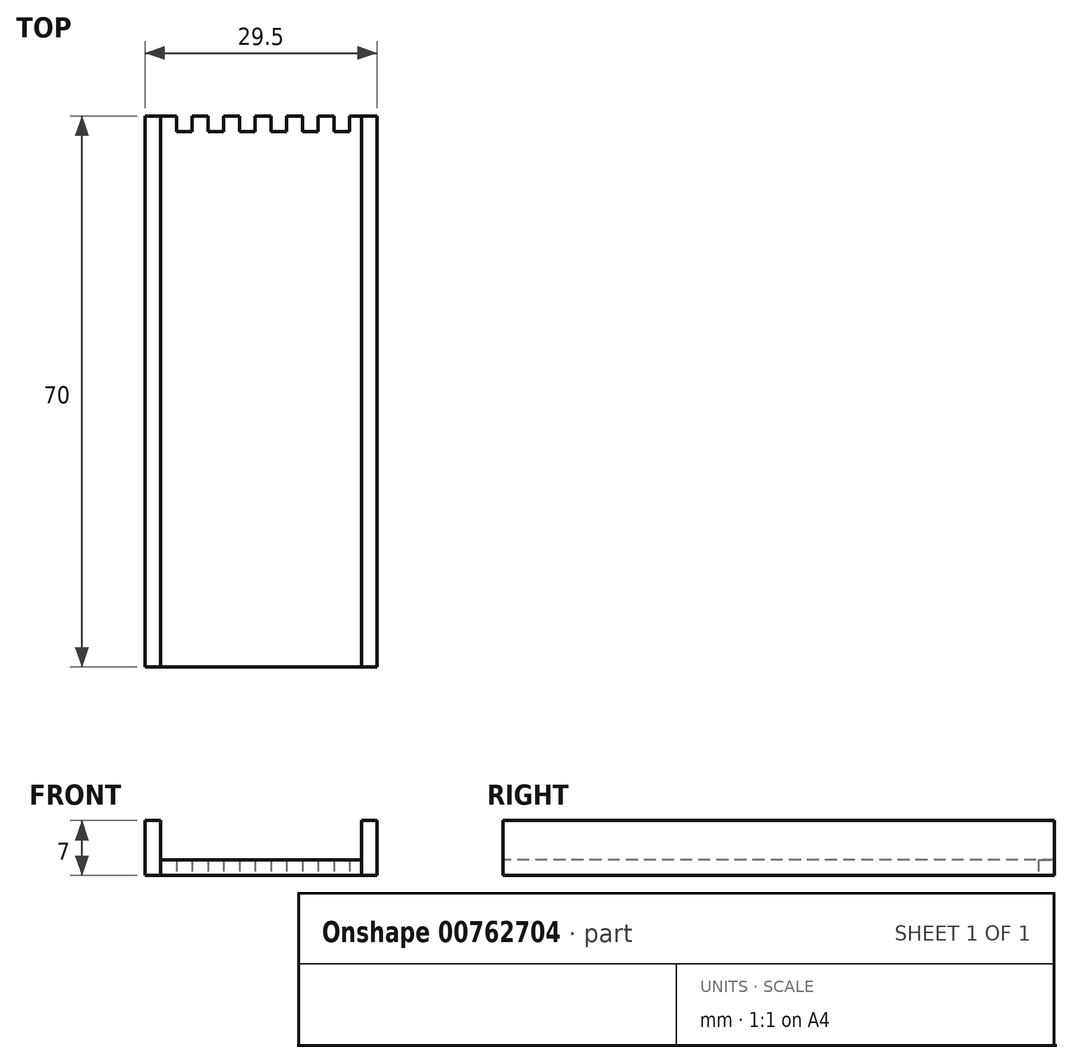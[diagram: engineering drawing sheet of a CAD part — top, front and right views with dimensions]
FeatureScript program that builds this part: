
annotation { "Feature Type Name" : "Feature", "Feature Type Description" : "" }
export const myFeature = defineFeature(function(context is Context, id is Id, definition is map)
    precondition{}
    {
        {
            var Q0;
            Q0=qCreatedBy(makeId("Top.planeOp"),FACE);
            var sketch = newSketch(context, id + "F0", { "sketchPlane" : qUnion([Q0])});
            skLineSegment(sketch, "E0.top", {"start": v(12.75, -35) * mm, "end": v(-12.75, -35) * mm});
            skLineSegment(sketch, "E0.left", {"start": v(12.75, 35) * mm, "end": v(12.75, -35) * mm});
            skLineSegment(sketch, "E0.right", {"start": v(-12.75, 35) * mm, "end": v(-12.75, -35) * mm});
            skPoint(sketch, "E0.middle", {"position": v(0, 0) * mm});
            skLineSegment(sketch, "E1", {"start": v(-12.75, 35) * mm, "end": v(-10.75, 35) * mm});
            skLineSegment(sketch, "E2", {"start": v(-10.75, 35) * mm, "end": v(-10.75, 33) * mm});
            skLineSegment(sketch, "E3", {"start": v(-10.75, 33) * mm, "end": v(-8.75, 33) * mm});
            skLineSegment(sketch, "E4", {"start": v(-8.75, 33) * mm, "end": v(-8.75, 35) * mm});
            skLineSegment(sketch, "E5", {"start": v(-8.75, 35) * mm, "end": v(-6.75, 35) * mm});
            skLineSegment(sketch, "E6", {"start": v(-6.75, 35) * mm, "end": v(-6.75, 33) * mm});
            skLineSegment(sketch, "E7", {"start": v(-6.75, 33) * mm, "end": v(-4.75, 33) * mm});
            skLineSegment(sketch, "E8", {"start": v(-4.75, 33) * mm, "end": v(-4.75, 35) * mm});
            skPoint(sketch, "E8.endSnap0", {"position": v(-7.75, 35) * mm});
            skLineSegment(sketch, "E9", {"start": v(-4.75, 35) * mm, "end": v(-2.75, 35) * mm});
            skLineSegment(sketch, "E10", {"start": v(-2.75, 35) * mm, "end": v(-2.75, 33) * mm});
            skLineSegment(sketch, "E11", {"start": v(-2.75, 33) * mm, "end": v(-0.75, 33) * mm});
            skLineSegment(sketch, "E12", {"start": v(-0.75, 33) * mm, "end": v(-0.75, 35) * mm});
            skLineSegment(sketch, "E13", {"start": v(-0.75, 35) * mm, "end": v(1.25, 35) * mm});
            skLineSegment(sketch, "E14", {"start": v(1.25, 35) * mm, "end": v(1.25, 33) * mm});
            skLineSegment(sketch, "E15", {"start": v(1.25, 33) * mm, "end": v(3.25, 33) * mm});
            skLineSegment(sketch, "E16", {"start": v(3.25, 33) * mm, "end": v(3.25, 35) * mm});
            skLineSegment(sketch, "E17", {"start": v(3.25, 35) * mm, "end": v(5.25, 35) * mm});
            skLineSegment(sketch, "E18", {"start": v(5.25, 35) * mm, "end": v(5.25, 33) * mm});
            skLineSegment(sketch, "E19", {"start": v(5.25, 33) * mm, "end": v(7.25, 33) * mm});
            skLineSegment(sketch, "E20", {"start": v(7.25, 33) * mm, "end": v(7.25, 35) * mm});
            skLineSegment(sketch, "E21", {"start": v(7.25, 35) * mm, "end": v(9.25, 35) * mm});
            skLineSegment(sketch, "E22", {"start": v(9.25, 35) * mm, "end": v(9.25, 33) * mm});
            skLineSegment(sketch, "E23", {"start": v(9.25, 33) * mm, "end": v(11.25, 33) * mm});
            skLineSegment(sketch, "E24", {"start": v(11.25, 33) * mm, "end": v(11.25, 35) * mm});
            skLineSegment(sketch, "E25", {"start": v(11.25, 35) * mm, "end": v(12.75, 35) * mm});
            skLineSegment(sketch, "E26", {"start": v(12.75, 35) * mm, "end": v(14.75, 35) * mm});
            skLineSegment(sketch, "E27", {"start": v(14.75, 35) * mm, "end": v(14.75, -35) * mm});
            skLineSegment(sketch, "E28", {"start": v(-12.75, 35) * mm, "end": v(-14.75, 35) * mm});
            skLineSegment(sketch, "E29", {"start": v(-14.75, 35) * mm, "end": v(-14.75, -35) * mm});
            skLineSegment(sketch, "E30", {"start": v(-14.75, -35) * mm, "end": v(-12.75, -35) * mm});
            skLineSegment(sketch, "E31", {"start": v(12.75, -35) * mm, "end": v(14.75, -35) * mm});
            skSolve(sketch);
        }
        {
            var Q0;
            Q0=makeQuery(id+"F0.imprint","IMPRINT",FACE,{"disambiguationData":[TD([[makeQuery(id+"F0.imprint","IMPRINT",EDGE,{"derivedFrom":sQuery(id+"F0.wireOp",EDGE,"E0.right")}),-1.0]])]});
            var Q1;
            Q1=makeQuery(id+"F0.imprint","IMPRINT",FACE,{"disambiguationData":[TD([[makeQuery(id+"F0.imprint","IMPRINT",EDGE,{"derivedFrom":sQuery(id+"F0.wireOp",EDGE,"E0.left")}),1.0]])]});
            extrude(context, id + "F1", {"entities" : qUnion([Q0, Q1]), "depth" : 7 * mm, "offsetDistance" : 25 * mm});
        }
        {
            var Q0;
            Q0=makeQuery(id+"F0.imprint","IMPRINT",FACE,{"disambiguationData":[TD([[makeQuery(id+"F0.imprint","IMPRINT",EDGE,{"derivedFrom":sQuery(id+"F0.wireOp",EDGE,"E0.top")}),-1.0]])]});
            extrude(context, id + "F2", {"entities" : qUnion([Q0]), "depth" : 2 * mm, "offsetDistance" : 25 * mm});
        }
    });
